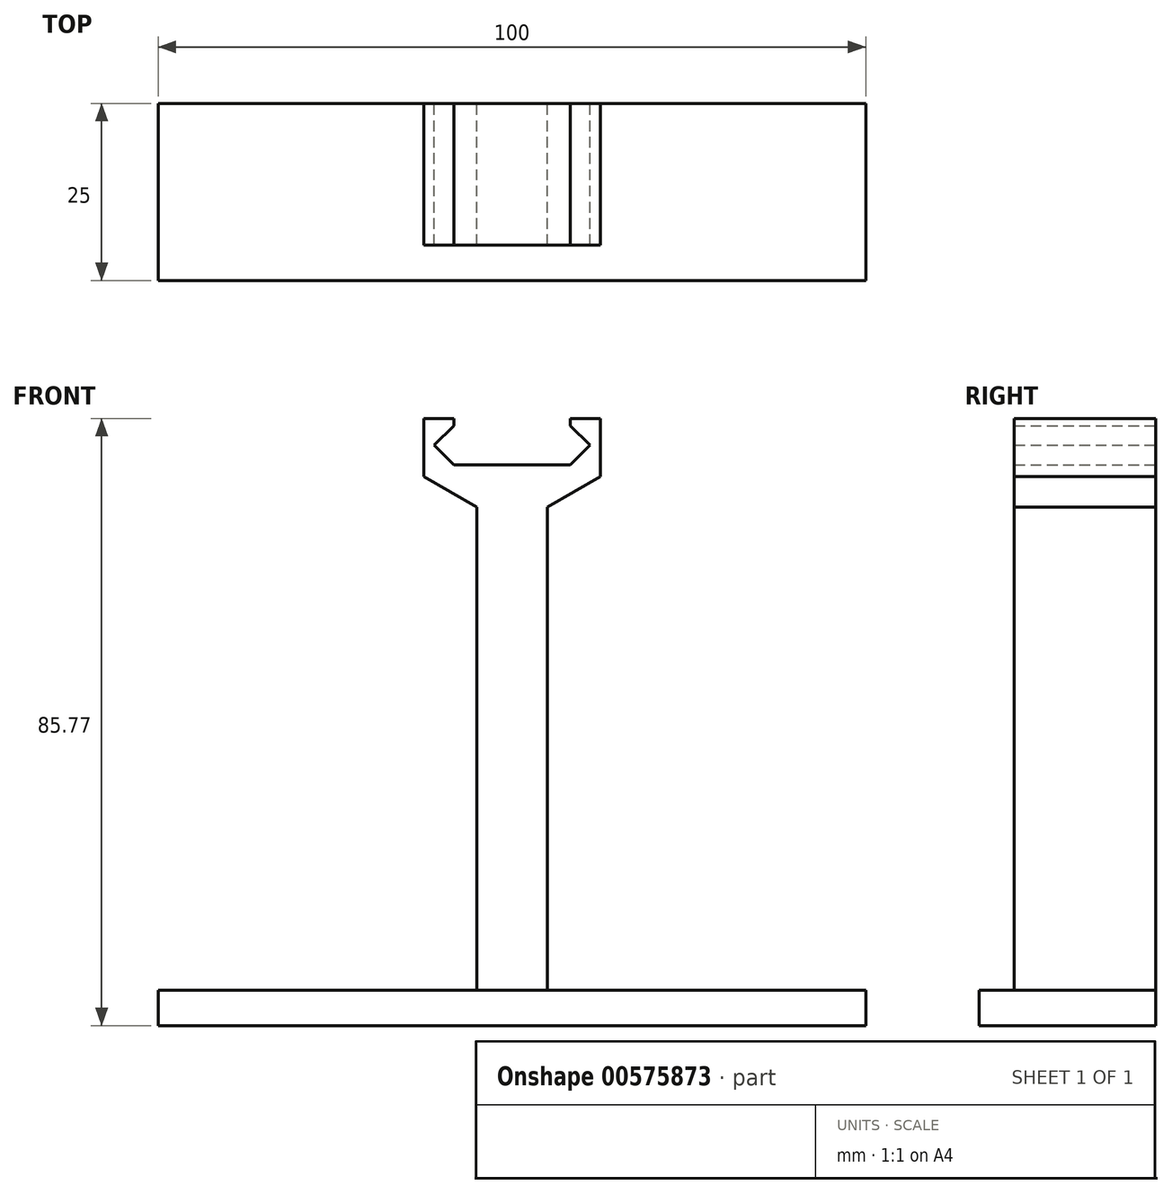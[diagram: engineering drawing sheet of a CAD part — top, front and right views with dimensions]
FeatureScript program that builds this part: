
annotation { "Feature Type Name" : "Feature", "Feature Type Description" : "" }
export const myFeature = defineFeature(function(context is Context, id is Id, definition is map)
    precondition{}
    {
        {
            var Q0;
            Q0=qCreatedBy(makeId("Front.planeOp"),FACE);
            var sketch = newSketch(context, id + "F0", { "sketchPlane" : qUnion([Q0])});
            skLineSegment(sketch, "E0.bottom", {"start": v(-50, 0) * mm, "end": v(50, 0) * mm});
            skLineSegment(sketch, "E0.top", {"start": v(-50, 5) * mm, "end": v(50, 5) * mm});
            skLineSegment(sketch, "E0.left", {"start": v(-50, 0) * mm, "end": v(-50, 5) * mm});
            skLineSegment(sketch, "E0.right", {"start": v(50, 0) * mm, "end": v(50, 5) * mm});
            skLineSegment(sketch, "E1.top", {"start": v(-5, 5) * mm, "end": v(5, 5) * mm});
            skLineSegment(sketch, "E1.left", {"start": v(-5, 73.23) * mm, "end": v(-5, 5) * mm});
            skLineSegment(sketch, "E1.right", {"start": v(5, 73.23) * mm, "end": v(5, 5) * mm});
            skLineSegment(sketch, "E2", {"start": v(0, 79.23) * mm, "end": v(8.24, 79.23) * mm});
            skLineSegment(sketch, "E3", {"start": v(8.24, 79.23) * mm, "end": v(11, 82) * mm});
            skLineSegment(sketch, "E4", {"start": v(11, 82) * mm, "end": v(8.24, 84.76) * mm});
            skLineSegment(sketch, "E5", {"start": v(8.24, 84.76) * mm, "end": v(8.24, 85.76) * mm});
            skLineSegment(sketch, "E6", {"start": v(8.24, 85.76) * mm, "end": v(12.5, 85.76) * mm});
            skLineSegment(sketch, "E7", {"start": v(12.5, 85.76) * mm, "end": v(12.5, 77.57) * mm});
            skLineSegment(sketch, "E8", {"start": v(12.5, 77.57) * mm, "end": v(5, 73.23) * mm});
            skLineSegment(sketch, "E9.MirrorCS", {"start": v(-8.24, 85.76) * mm, "end": v(-12.5, 85.76) * mm});
            skLineSegment(sketch, "E10.MirrorCS", {"start": v(-8.23, 84.76) * mm, "end": v(-8.23, 85.76) * mm});
            skLineSegment(sketch, "E11.MirrorCS", {"start": v(-11, 82) * mm, "end": v(-8.23, 84.76) * mm});
            skLineSegment(sketch, "E12.MirrorCS", {"start": v(-8.23, 79.23) * mm, "end": v(-11, 82) * mm});
            skLineSegment(sketch, "E13.MirrorCS", {"start": v(0, 79.23) * mm, "end": v(-8.23, 79.23) * mm});
            skLineSegment(sketch, "E14.MirrorCS", {"start": v(-12.5, 77.57) * mm, "end": v(-5, 73.23) * mm});
            skLineSegment(sketch, "E15.MirrorCS", {"start": v(-12.5, 85.76) * mm, "end": v(-12.5, 77.57) * mm});
            skSolve(sketch);
        }
        {
            var Q0;
            Q0 = qSketchRegion(id + "F0", true);
            extrude(context, id + "F1", {"entities" : qUnion([Q0]), "depth" : 20 * mm, "offsetDistance" : 25 * mm});
        }
        {
            var Q0;
            Q0=makeQuery(id+"F1.opExtrude","CAP_FACE",FACE,{"disambiguationData":[OSD([sQuery(id+"F0.wireOp",EDGE,"E0.bottom"),sQuery(id+"F0.wireOp",EDGE,"E0.top"),sQuery(id+"F0.wireOp",EDGE,"E0.left"),sQuery(id+"F0.wireOp",EDGE,"E0.right"),sQuery(id+"F0.wireOp",EDGE,"E1.left"),sQuery(id+"F0.wireOp",EDGE,"E1.right"),sQuery(id+"F0.wireOp",EDGE,"E2"),sQuery(id+"F0.wireOp",EDGE,"E3"),sQuery(id+"F0.wireOp",EDGE,"E4"),sQuery(id+"F0.wireOp",EDGE,"E5"),sQuery(id+"F0.wireOp",EDGE,"E6"),sQuery(id+"F0.wireOp",EDGE,"E7"),sQuery(id+"F0.wireOp",EDGE,"E8"),sQuery(id+"F0.wireOp",EDGE,"E9.MirrorCS"),sQuery(id+"F0.wireOp",EDGE,"E10.MirrorCS"),sQuery(id+"F0.wireOp",EDGE,"E11.MirrorCS"),sQuery(id+"F0.wireOp",EDGE,"E12.MirrorCS"),sQuery(id+"F0.wireOp",EDGE,"E13.MirrorCS"),sQuery(id+"F0.wireOp",EDGE,"E14.MirrorCS"),sQuery(id+"F0.wireOp",EDGE,"E15.MirrorCS")])],"isStart":false});
            var sketch = newSketch(context, id + "F2", { "sketchPlane" : qUnion([Q0])});
            skLineSegment(sketch, "E16.bottom", {"start": v(-50, 5) * mm, "end": v(50, 5) * mm});
            skLineSegment(sketch, "E16.top", {"start": v(-50, 0) * mm, "end": v(50, 0) * mm});
            skLineSegment(sketch, "E16.left", {"start": v(-50, 5) * mm, "end": v(-50, 0) * mm});
            skLineSegment(sketch, "E16.right", {"start": v(50, 5) * mm, "end": v(50, 0) * mm});
            skSolve(sketch);
        }
        {
            var Q0;
            Q0=makeQuery(id+"F2.imprint","IMPRINT",FACE,{"disambiguationData":[TD([[makeQuery(id+"F2.imprint","IMPRINT",EDGE,{"derivedFrom":sQuery(id+"F2.wireOp",EDGE,"E16.top")}),1.0]])]});
            extrude(context, id + "F3", {"entities" : qUnion([Q0]), "operationType" : NewBodyOperationType.ADD, "depth" : 5 * mm, "offsetDistance" : 25 * mm});
        }
    });
